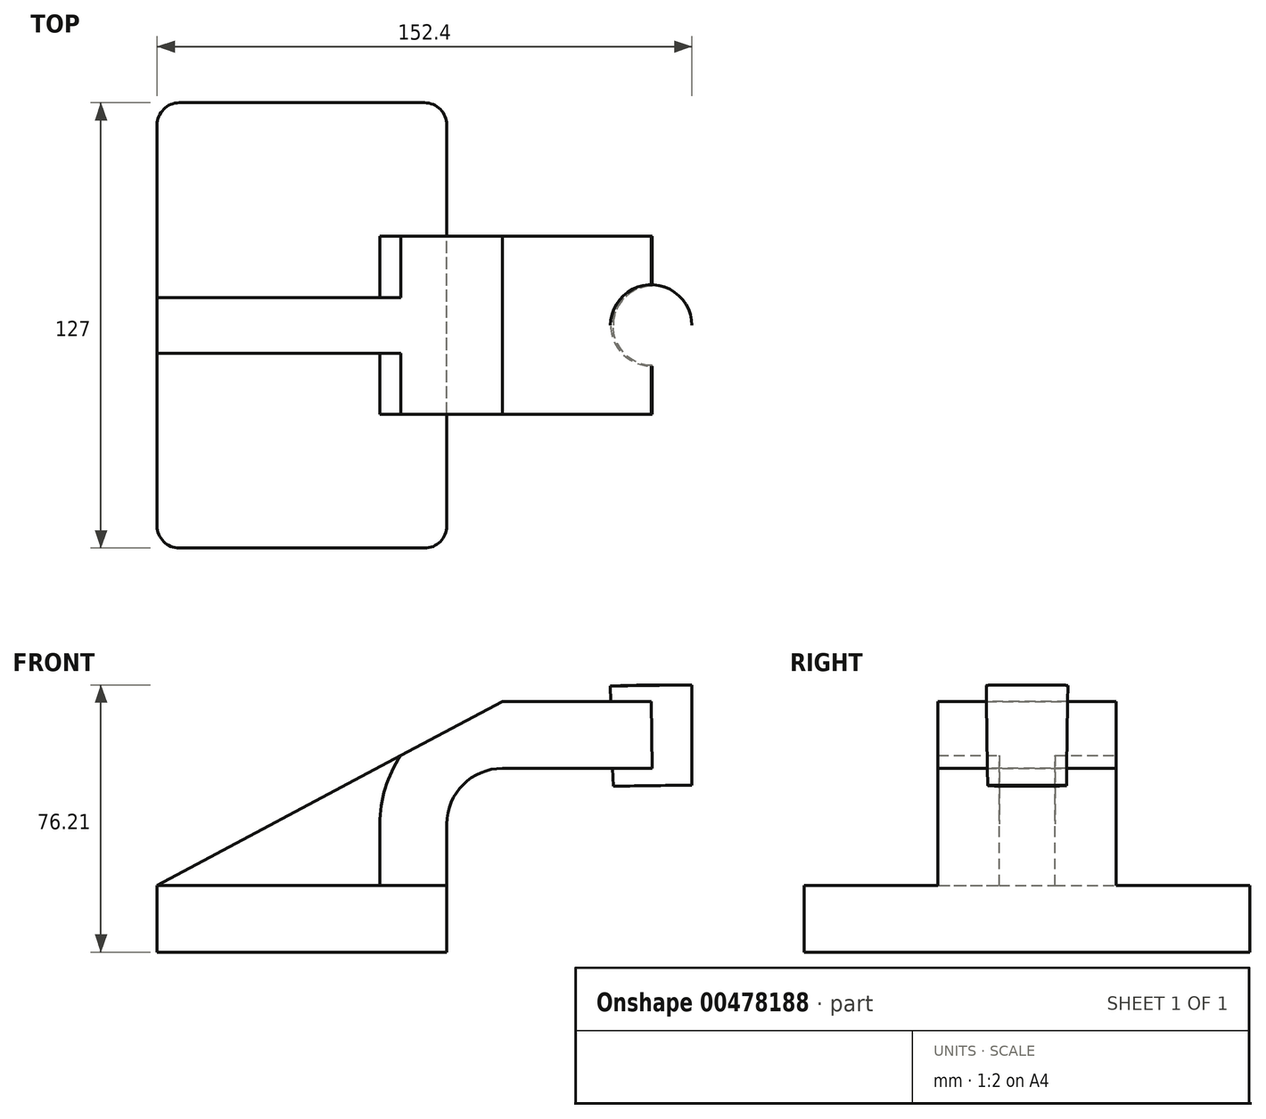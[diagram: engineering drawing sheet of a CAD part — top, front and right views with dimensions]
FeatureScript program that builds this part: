
annotation { "Feature Type Name" : "Feature", "Feature Type Description" : "" }
export const myFeature = defineFeature(function(context is Context, id is Id, definition is map)
    precondition{}
    {
        {
            var Q0;
            Q0=qCreatedBy(makeId("Front.planeOp"),FACE);
            var sketch = newSketch(context, id + "F0", { "sketchPlane" : qUnion([Q0])});
            skLineSegment(sketch, "E0.bottom", {"start": v(41.27, 9.53) * mm, "end": v(-41.27, 9.53) * mm});
            skLineSegment(sketch, "E0.top", {"start": v(41.28, -9.52) * mm, "end": v(-41.27, -9.52) * mm});
            skLineSegment(sketch, "E0.left", {"start": v(41.28, 9.53) * mm, "end": v(41.28, -9.52) * mm});
            skLineSegment(sketch, "E0.right", {"start": v(-41.27, 9.53) * mm, "end": v(-41.27, -9.52) * mm});
            skPoint(sketch, "E0.middle", {"position": v(0, 0) * mm});
            skLineSegment(sketch, "E1.bottom", {"start": v(111.12, 38.1) * mm, "end": v(60.32, 38.1) * mm});
            skLineSegment(sketch, "E1.top", {"start": v(111.12, 66.68) * mm, "end": v(60.32, 66.68) * mm});
            skLineSegment(sketch, "E1.left", {"start": v(111.12, 38.1) * mm, "end": v(111.12, 66.68) * mm});
            skLineSegment(sketch, "E1.right", {"start": v(60.32, 38.1) * mm, "end": v(60.32, 66.68) * mm});
            skPoint(sketch, "E1.middle", {"position": v(85.72, 52.39) * mm});
            skLineSegment(sketch, "E2", {"start": v(41.27, 9.53) * mm, "end": v(41.27, 27) * mm});
            skArc(sketch, "E3", {"start": v(41.27, 27) * mm, "mid": v(45.92, 38.23) * mm, "end": v(57.15, 42.88) * mm});
            skLineSegment(sketch, "E4", {"start": v(57.15, 42.88) * mm, "end": v(99.9, 42.88) * mm});
            skLineSegment(sketch, "E5.0", {"start": v(57.15, 61.93) * mm, "end": v(99.9, 61.93) * mm});
            skArc(sketch, "E5.1", {"start": v(22.22, 27) * mm, "mid": v(32.45, 51.7) * mm, "end": v(57.15, 61.93) * mm});
            skLineSegment(sketch, "E5.2", {"start": v(22.22, 9.53) * mm, "end": v(22.22, 27) * mm});
            skLineSegment(sketch, "E6", {"start": v(99.5, 66.68) * mm, "end": v(99.9, 38.1) * mm});
            skLineSegment(sketch, "E7", {"start": v(-41.27, 9.53) * mm, "end": v(57.15, 61.93) * mm});
            skSolve(sketch);
        }
        {
            var Q0;
            Q0=makeQuery(id+"F0.imprint","IMPRINT",FACE,{"disambiguationData":[TD([[makeQuery(id+"F0.imprint","IMPRINT",EDGE,{"derivedFrom":sQuery(id+"F0.wireOp",EDGE,"E0.top")}),-1.0]])]});
            extrude(context, id + "F1", {"entities" : qUnion([Q0]), "endBound" : BoundingType.SYMMETRIC, "depth" : 127 * mm});
        }
        {
            var Q0;
            {var subQ1=sQuery(id+"F0.wireOp",EDGE,"E2");Q0=makeQuery(id+"F0.imprint","IMPRINT",FACE,{"disambiguationData":[TD([[makeQuery(id+"F0.imprint","IMPRINT",EDGE,{"derivedFrom":subQ1}),1.0]])]});}
            var Q1;
            {var subQ0=sQuery(id+"F0.wireOp",EDGE,"E4");var subQ1=sQuery(id+"F0.wireOp",EDGE,"E1.right");var subQ2=makeQuery(id+"F0.imprint","INTERSECT",VERTEX,{"derivedFrom":[subQ1,subQ0]});Q1=makeQuery(id+"F0.imprint","IMPRINT",FACE,{"disambiguationData":[TD([[makeQuery(id+"F0.imprint","IMPRINT",EDGE,{"disambiguationData":[TD([[subQ2,-1.0]])],"derivedFrom":subQ1}),-1.0]])]});}
            extrude(context, id + "F2", {"entities" : qUnion([Q0, Q1]), "operationType" : NewBodyOperationType.ADD, "endBound" : BoundingType.SYMMETRIC, "depth" : 50.8 * mm});
        }
        {
            var Q0;
            {var subQ3=sQuery(id+"F0.wireOp",EDGE,"E5.2");Q0=makeQuery(id+"F0.imprint","IMPRINT",FACE,{"disambiguationData":[TD([[makeQuery(id+"F0.imprint","IMPRINT",EDGE,{"derivedFrom":subQ3}),1.0]])]});}
            extrude(context, id + "F3", {"entities" : qUnion([Q0]), "operationType" : NewBodyOperationType.ADD, "endBound" : BoundingType.SYMMETRIC, "depth" : 15.88 * mm});
        }
        {
            var Q0;
            {var subQ0=sQuery(id+"F0.wireOp",EDGE,"E1.left");Q0=makeQuery(id+"F0.imprint","IMPRINT",FACE,{"disambiguationData":[TD([[makeQuery(id+"F0.imprint","IMPRINT",EDGE,{"derivedFrom":subQ0}),1.0]])]});}
            var Q1;
            Q1=sQuery(id+"F0.wireOp",EDGE,"E6");
            revolve(context, id + "F4", {"operationType" : NewBodyOperationType.ADD, "entities" : qUnion([Q0]), "axis" : qUnion([Q1]), "revolveType" : RevolveType.FULL});
        }
        {
            var Q0;
            Q0=makeQuery(id+"F1.opExtrude","CAP_EDGE",EDGE,{"disambiguationData":[OSD([sQuery(id+"F0.wireOp",EDGE,"E0.left")])],"isStart":false});
            var Q1;
            Q1=makeQuery(id+"F1.opExtrude","CAP_EDGE",EDGE,{"disambiguationData":[OSD([sQuery(id+"F0.wireOp",EDGE,"E0.right")])],"isStart":false});
            var Q2;
            Q2=makeQuery(id+"F1.opExtrude","CAP_EDGE",EDGE,{"disambiguationData":[OSD([sQuery(id+"F0.wireOp",EDGE,"E0.left")])],"isStart":true});
            var Q3;
            Q3=makeQuery(id+"F1.opExtrude","CAP_EDGE",EDGE,{"disambiguationData":[OSD([sQuery(id+"F0.wireOp",EDGE,"E0.right")])],"isStart":true});
            fillet(context, id + "F5", {"entities" : qUnion([Q0, Q1, Q2, Q3]), "radius" : 6.35 * mm, "tangentPropagation" : true, "allowEdgeOverflow" : false});
        }
    });
